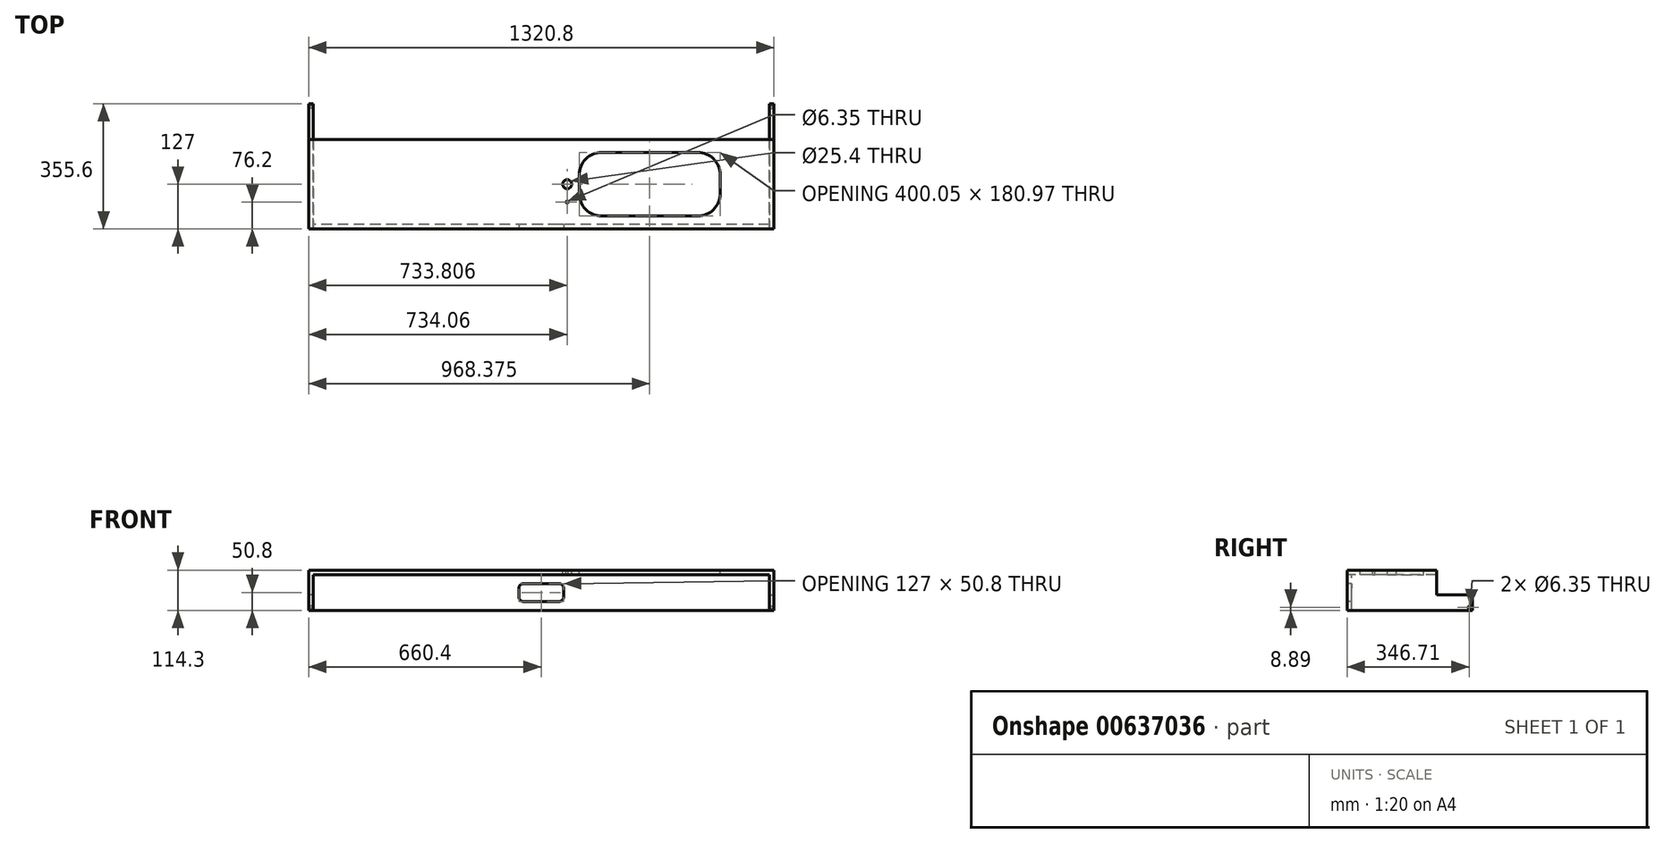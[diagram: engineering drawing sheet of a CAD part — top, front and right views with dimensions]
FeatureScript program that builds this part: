
annotation { "Feature Type Name" : "Feature", "Feature Type Description" : "" }
export const myFeature = defineFeature(function(context is Context, id is Id, definition is map)
    precondition{}
    {
        {
            var Q0;
            Q0=qCreatedBy(makeId("Top.planeOp"),FACE);
            var sketch = newSketch(context, id + "F0", { "sketchPlane" : qUnion([Q0])});
            skLineSegment(sketch, "E0.bottom", {"start": v(-660.4, 127) * mm, "end": v(660.4, 127) * mm});
            skLineSegment(sketch, "E0.top", {"start": v(-660.4, -127) * mm, "end": v(660.4, -127) * mm});
            skLineSegment(sketch, "E0.left", {"start": v(-660.4, 127) * mm, "end": v(-660.4, -127) * mm});
            skLineSegment(sketch, "E0.right", {"start": v(660.4, 127) * mm, "end": v(660.4, -127) * mm});
            skSolve(sketch);
        }
        {
            var Q0;
            Q0=makeQuery(id+"F0.imprint","IMPRINT",FACE,{"disambiguationData":[TD([[makeQuery(id+"F0.imprint","IMPRINT",EDGE,{"derivedFrom":sQuery(id+"F0.wireOp",EDGE,"E0.bottom")}),-1.0]])]});
            var Q1;
            Q1 = qConstructionFilter(qBodyType(qCreatedBy(id + "F0" ,EDGE), BodyType.WIRE), ConstructionObject.NO);
            extrude(context, id + "F1", {"entities" : qUnion([Q0]), "surfaceEntities" : qUnion([Q1]), "oppositeDirection" : true, "depth" : 12.7 * mm, "offsetDistance" : 25.4 * mm});
        }
        {
            var Q0;
            Q0=makeQuery(id+"F1.opExtrude","SWEPT_FACE",FACE,{"disambiguationData":[OSD([sQuery(id+"F0.wireOp",EDGE,"E0.right")])]});
            cPlane(context, id + "F2", {"entities" : qUnion([Q0]), "cplaneType" : CPlaneType.OFFSET, "offset" : 0 * mm, "width" : 152.4 * mm, "height" : 152.4 * mm});
        }
        {
            var Q0;
            Q0=qCreatedBy(id+"F2.planeOp",FACE);
            var sketch = newSketch(context, id + "F3", { "sketchPlane" : qUnion([Q0])});
            skLineSegment(sketch, "E1", {"start": v(-127, -114.3) * mm, "end": v(228.6, -114.3) * mm});
            skLineSegment(sketch, "E2", {"start": v(127, -12.7) * mm, "end": v(0, -12.7) * mm});
            skLineSegment(sketch, "E3", {"start": v(127, -12.7) * mm, "end": v(127, -69.85) * mm});
            skLineSegment(sketch, "E4", {"start": v(127, -69.85) * mm, "end": v(228.6, -69.85) * mm});
            skLineSegment(sketch, "E5", {"start": v(228.6, -69.85) * mm, "end": v(228.6, -114.3) * mm});
            skLineSegment(sketch, "E6", {"start": v(-127, -114.3) * mm, "end": v(-127, -12.7) * mm});
            skLineSegment(sketch, "E7", {"start": v(-127, -12.7) * mm, "end": v(127, -12.7) * mm});
            skPoint(sketch, "E8", {"position": v(219.71, -105.41) * mm});
            skSolve(sketch);
        }
        {
            var Q0;
            Q0 = qSketchRegion(id + "F3", true);
            extrude(context, id + "F4", {"entities" : qUnion([Q0]), "oppositeDirection" : true, "depth" : 12.7 * mm, "offsetDistance" : 25.4 * mm});
        }
        {
            var Q0;
            Q0=sQuery(id+"F3.wireOp",VERTEX,"E8");
            var Q1;
            Q1=makeQuery(id+"F4.opExtrude","SWEPT_BODY",BODY,{"disambiguationData":[OSD([sQuery(id+"F3.wireOp",EDGE,"E1"),sQuery(id+"F3.wireOp",EDGE,"E3"),sQuery(id+"F3.wireOp",EDGE,"E4"),sQuery(id+"F3.wireOp",EDGE,"E5"),sQuery(id+"F3.wireOp",EDGE,"E6"),sQuery(id+"F3.wireOp",EDGE,"E7")])]});
            hole(context, id + "F5", {"style" : HoleStyle.SIMPLE, "endStyle" : HoleEndStyle.THROUGH, "holeDiameter" : 6.35 * mm, "majorDiameter" : 6.35 * mm, "isTappedThrough" : true, "tappedDepth" : 12.7 * mm, "tapClearance" : 3, "locations" : qUnion([Q0]), "scope" : qUnion([Q1])});
        }
        {
            var Q0;
            Q0=makeQuery(id+"F4.opExtrude","SWEPT_BODY",BODY,{"disambiguationData":[OSD([sQuery(id+"F3.wireOp",EDGE,"E1"),sQuery(id+"F3.wireOp",EDGE,"E3"),sQuery(id+"F3.wireOp",EDGE,"E4"),sQuery(id+"F3.wireOp",EDGE,"E5"),sQuery(id+"F3.wireOp",EDGE,"E6"),sQuery(id+"F3.wireOp",EDGE,"E7")])]});
            var Q1;
            Q1=qCreatedBy(makeId("Right.planeOp"),FACE);
            mirror(context, id + "F6", {"operationType" : NewBodyOperationType.ADD, "entities" : qUnion([Q0]), "mirrorPlane" : qUnion([Q1])});
        }
        {
            var Q0;
            Q0=qCreatedBy(makeId("Top.planeOp"),FACE);
            var sketch = newSketch(context, id + "F7", { "sketchPlane" : qUnion([Q0])});
            skLineSegment(sketch, "E9.bottom", {"start": v(444.5, 90.49) * mm, "end": v(171.45, 90.49) * mm});
            skLineSegment(sketch, "E9.top", {"start": v(444.5, -90.49) * mm, "end": v(171.45, -90.49) * mm});
            skLineSegment(sketch, "E9.left", {"start": v(508, 26.99) * mm, "end": v(508, -26.99) * mm});
            skLineSegment(sketch, "E9.right", {"start": v(107.95, 26.99) * mm, "end": v(107.95, -26.99) * mm});
            skPoint(sketch, "E9.middle", {"position": v(307.98, 0) * mm});
            skPoint(sketch, "E10.visualSharp", {"position": v(107.95, 90.49) * mm});
            skArc(sketch, "E10.filletArc", {"start": v(171.45, 90.49) * mm, "mid": v(126.55, 71.89) * mm, "end": v(107.95, 26.99) * mm});
            skPoint(sketch, "E11.visualSharp", {"position": v(107.95, -90.49) * mm});
            skArc(sketch, "E11.filletArc", {"start": v(107.95, -26.99) * mm, "mid": v(126.55, -71.89) * mm, "end": v(171.45, -90.49) * mm});
            skPoint(sketch, "E12.visualSharp", {"position": v(508, 90.49) * mm});
            skArc(sketch, "E12.filletArc", {"start": v(508, 26.99) * mm, "mid": v(489.4, 71.89) * mm, "end": v(444.5, 90.49) * mm});
            skPoint(sketch, "E13.visualSharp", {"position": v(508, -90.49) * mm});
            skArc(sketch, "E13.filletArc", {"start": v(444.5, -90.49) * mm, "mid": v(489.4, -71.89) * mm, "end": v(508, -26.99) * mm});
            skSolve(sketch);
        }
        {
            var Q0;
            Q0 = qSketchRegion(id + "F7", true);
            extrude(context, id + "F8", {"entities" : qUnion([Q0]), "operationType" : NewBodyOperationType.REMOVE, "endBound" : BoundingType.THROUGH_ALL, "oppositeDirection" : true, "depth" : 25.4 * mm, "offsetDistance" : 25.4 * mm});
        }
        {
            var Q0;
            Q0=qCreatedBy(makeId("Top.planeOp"),FACE);
            var sketch = newSketch(context, id + "F9", { "sketchPlane" : qUnion([Q0])});
            skCircle(sketch, "E14", {"center": v(73.66, 0) * mm, "radius": 12.7 * mm});
            skCircle(sketch, "E15", {"center": v(73.4, -50.8) * mm, "radius": 3.18 * mm});
            skSolve(sketch);
        }
        {
            var Q0;
            Q0 = qSketchRegion(id + "F9", true);
            extrude(context, id + "F10", {"entities" : qUnion([Q0]), "operationType" : NewBodyOperationType.REMOVE, "endBound" : BoundingType.THROUGH_ALL, "oppositeDirection" : true, "depth" : 25.4 * mm, "offsetDistance" : 25.4 * mm});
        }
        {
            var Q0;
            Q0=makeQuery(id+"F1.opExtrude","SWEPT_FACE",FACE,{"disambiguationData":[OSD([sQuery(id+"F0.wireOp",EDGE,"E0.top")])]});
            cPlane(context, id + "F11", {"entities" : qUnion([Q0]), "cplaneType" : CPlaneType.OFFSET, "offset" : 0 * mm, "width" : 152.4 * mm, "height" : 152.4 * mm});
        }
        {
            var Q0;
            Q0=qCreatedBy(id+"F11.planeOp",FACE);
            var sketch = newSketch(context, id + "F12", { "sketchPlane" : qUnion([Q0])});
            skLineSegment(sketch, "E16.bottom", {"start": v(647.7, -114.3) * mm, "end": v(-647.7, -114.3) * mm});
            skLineSegment(sketch, "E16.top", {"start": v(647.7, -12.7) * mm, "end": v(-647.7, -12.7) * mm});
            skLineSegment(sketch, "E16.left", {"start": v(647.7, -114.3) * mm, "end": v(647.7, -12.7) * mm});
            skLineSegment(sketch, "E16.right", {"start": v(-647.7, -114.3) * mm, "end": v(-647.7, -12.7) * mm});
            skPoint(sketch, "E16.middle", {"position": v(0, -63.5) * mm});
            skLineSegment(sketch, "E17.bottom", {"start": v(50.8, -88.9) * mm, "end": v(-50.8, -88.9) * mm});
            skLineSegment(sketch, "E17.top", {"start": v(50.8, -38.1) * mm, "end": v(-50.8, -38.1) * mm});
            skLineSegment(sketch, "E17.left", {"start": v(63.5, -76.2) * mm, "end": v(63.5, -50.8) * mm});
            skLineSegment(sketch, "E17.right", {"start": v(-63.5, -76.2) * mm, "end": v(-63.5, -50.8) * mm});
            skPoint(sketch, "E18.visualSharp", {"position": v(-63.5, -38.1) * mm});
            skArc(sketch, "E18.filletArc", {"start": v(-50.8, -38.1) * mm, "mid": v(-59.78, -41.82) * mm, "end": v(-63.5, -50.8) * mm});
            skPoint(sketch, "E19.visualSharp", {"position": v(-63.5, -88.9) * mm});
            skArc(sketch, "E19.filletArc", {"start": v(-63.5, -76.2) * mm, "mid": v(-59.78, -85.18) * mm, "end": v(-50.8, -88.9) * mm});
            skPoint(sketch, "E20.visualSharp", {"position": v(63.5, -38.1) * mm});
            skArc(sketch, "E20.filletArc", {"start": v(63.5, -50.8) * mm, "mid": v(59.78, -41.82) * mm, "end": v(50.8, -38.1) * mm});
            skPoint(sketch, "E21.visualSharp", {"position": v(63.5, -88.9) * mm});
            skArc(sketch, "E21.filletArc", {"start": v(50.8, -88.9) * mm, "mid": v(59.78, -85.18) * mm, "end": v(63.5, -76.2) * mm});
            skSolve(sketch);
        }
        {
            var Q0;
            Q0=makeQuery(id+"F12.imprint","IMPRINT",FACE,{"disambiguationData":[TD([[makeQuery(id+"F12.imprint","IMPRINT",EDGE,{"derivedFrom":sQuery(id+"F12.wireOp",EDGE,"E16.bottom")}),-1.0]])]});
            extrude(context, id + "F13", {"entities" : qUnion([Q0]), "oppositeDirection" : true, "depth" : 12.7 * mm, "offsetDistance" : 25.4 * mm});
        }
    });
